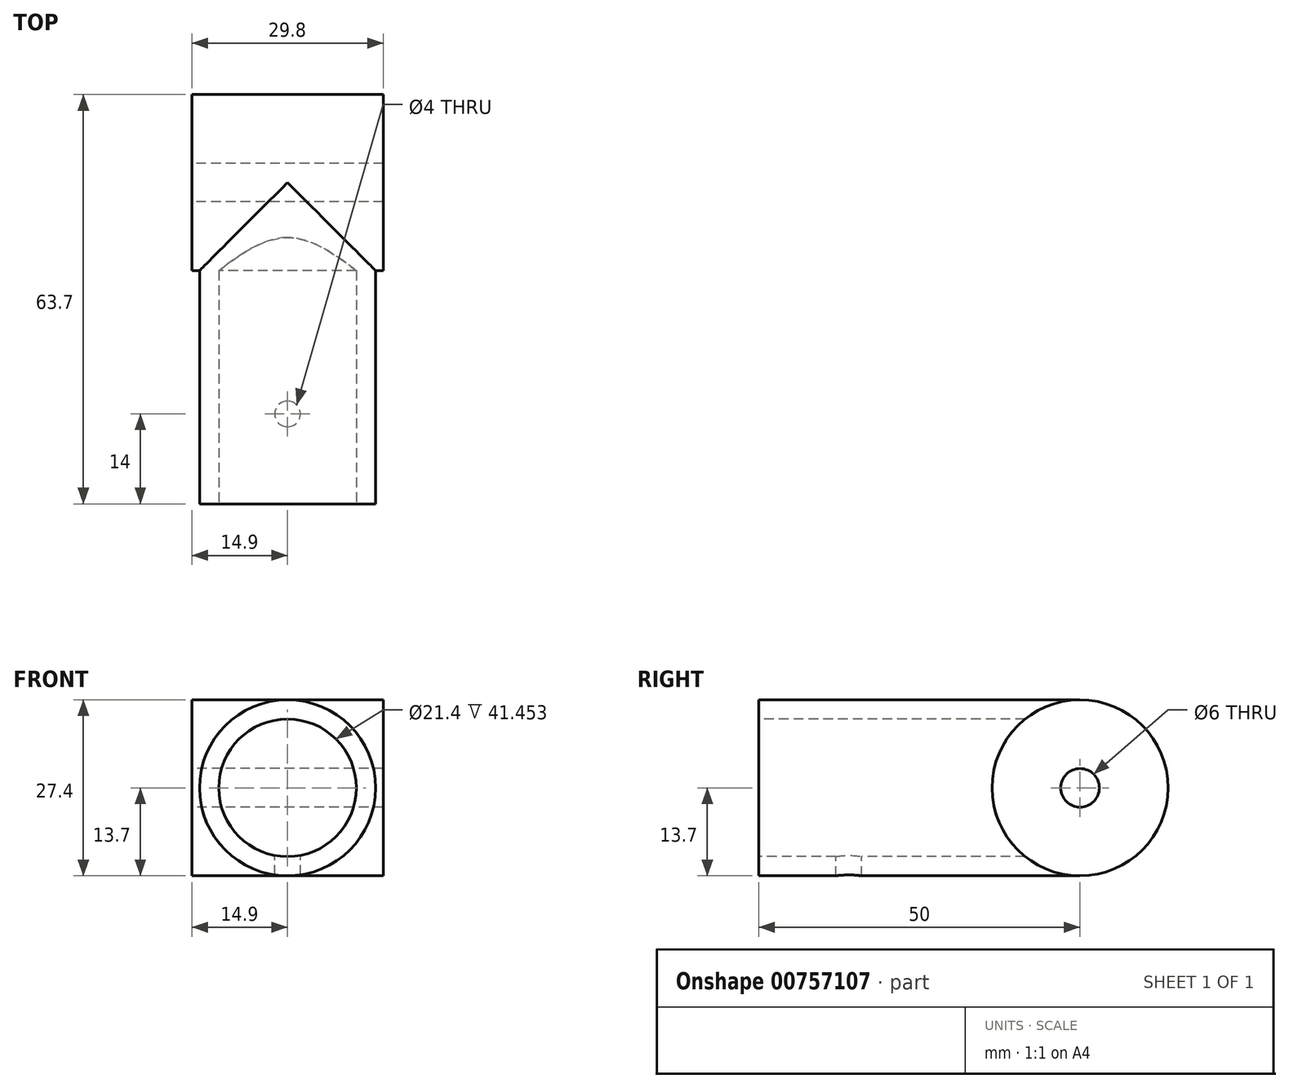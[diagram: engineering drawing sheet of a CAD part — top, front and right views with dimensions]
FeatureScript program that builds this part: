
annotation { "Feature Type Name" : "Feature", "Feature Type Description" : "" }
export const myFeature = defineFeature(function(context is Context, id is Id, definition is map)
    precondition{}
    {
        {
            var Q0;
            Q0=qCreatedBy(makeId("Front.planeOp"),FACE);
            cPlane(context, id + "F0", {"entities" : qUnion([Q0]), "cplaneType" : CPlaneType.OFFSET, "offset" : 50 * mm, "width" : 150 * mm, "height" : 150 * mm});
        }
        {
            var Q0;
            Q0=qCreatedBy(id+"F0.planeOp",FACE);
            var sketch = newSketch(context, id + "F1", { "sketchPlane" : qUnion([Q0])});
            skCircle(sketch, "E0", {"center": v(0, 0) * mm, "radius": 13.7 * mm});
            skCircle(sketch, "E1", {"center": v(0, 0) * mm, "radius": 10.7 * mm});
            skSolve(sketch);
        }
        {
            var Q0;
            Q0=qCreatedBy(makeId("Right.planeOp"),FACE);
            var sketch = newSketch(context, id + "F2", { "sketchPlane" : qUnion([Q0])});
            skCircle(sketch, "E2", {"center": v(0, 0) * mm, "radius": 13.7 * mm});
            skCircle(sketch, "E3", {"center": v(0, 0) * mm, "radius": 3 * mm});
            skSolve(sketch);
        }
        {
            var Q0;
            Q0=makeQuery(id+"F2.imprint","IMPRINT",FACE,{"disambiguationData":[TD([[makeQuery(id+"F2.imprint","IMPRINT",EDGE,{"derivedFrom":sQuery(id+"F2.wireOp",EDGE,"E2")}),1.0]])]});
            extrude(context, id + "F3", {"entities" : qUnion([Q0]), "endBound" : BoundingType.SYMMETRIC, "depth" : 29.8 * mm, "offsetDistance" : 25 * mm});
        }
        {
            var Q0;
            Q0=makeQuery(id+"F1.imprint","IMPRINT",FACE,{"disambiguationData":[TD([[makeQuery(id+"F1.imprint","IMPRINT",EDGE,{"derivedFrom":sQuery(id+"F1.wireOp",EDGE,"E0")}),1.0]])]});
            extrude(context, id + "F4", {"entities" : qUnion([Q0]), "operationType" : NewBodyOperationType.ADD, "endBound" : BoundingType.UP_TO_NEXT, "oppositeDirection" : true, "depth" : 25 * mm, "offsetDistance" : 25 * mm});
        }
        {
            var Q0;
            Q0=qCreatedBy(makeId("Top.planeOp"),FACE);
            var sketch = newSketch(context, id + "F5", { "sketchPlane" : qUnion([Q0])});
            skLineSegment(sketch, "E4", {"start": v(0, 0) * mm, "end": v(0, -36) * mm, "construction": true});
            skSolve(sketch);
        }
        {
            var Q0;
            Q0=sQuery(id+"F5.wireOp",VERTEX,"E4.end");
            var Q1;
            Q1=makeQuery(id+"F3.opExtrude","SWEPT_BODY",BODY,{"disambiguationData":[OSD([sQuery(id+"F2.wireOp",EDGE,"E2"),sQuery(id+"F2.wireOp",EDGE,"E3")])]});
            hole(context, id + "F6", {"style" : HoleStyle.SIMPLE, "endStyle" : HoleEndStyle.THROUGH, "holeDiameter" : 4 * mm, "majorDiameter" : 5 * mm, "isTappedThrough" : true, "tappedDepth" : 12 * mm, "tapClearance" : 3, "locations" : qUnion([Q0]), "scope" : qUnion([Q1])});
        }
    });
